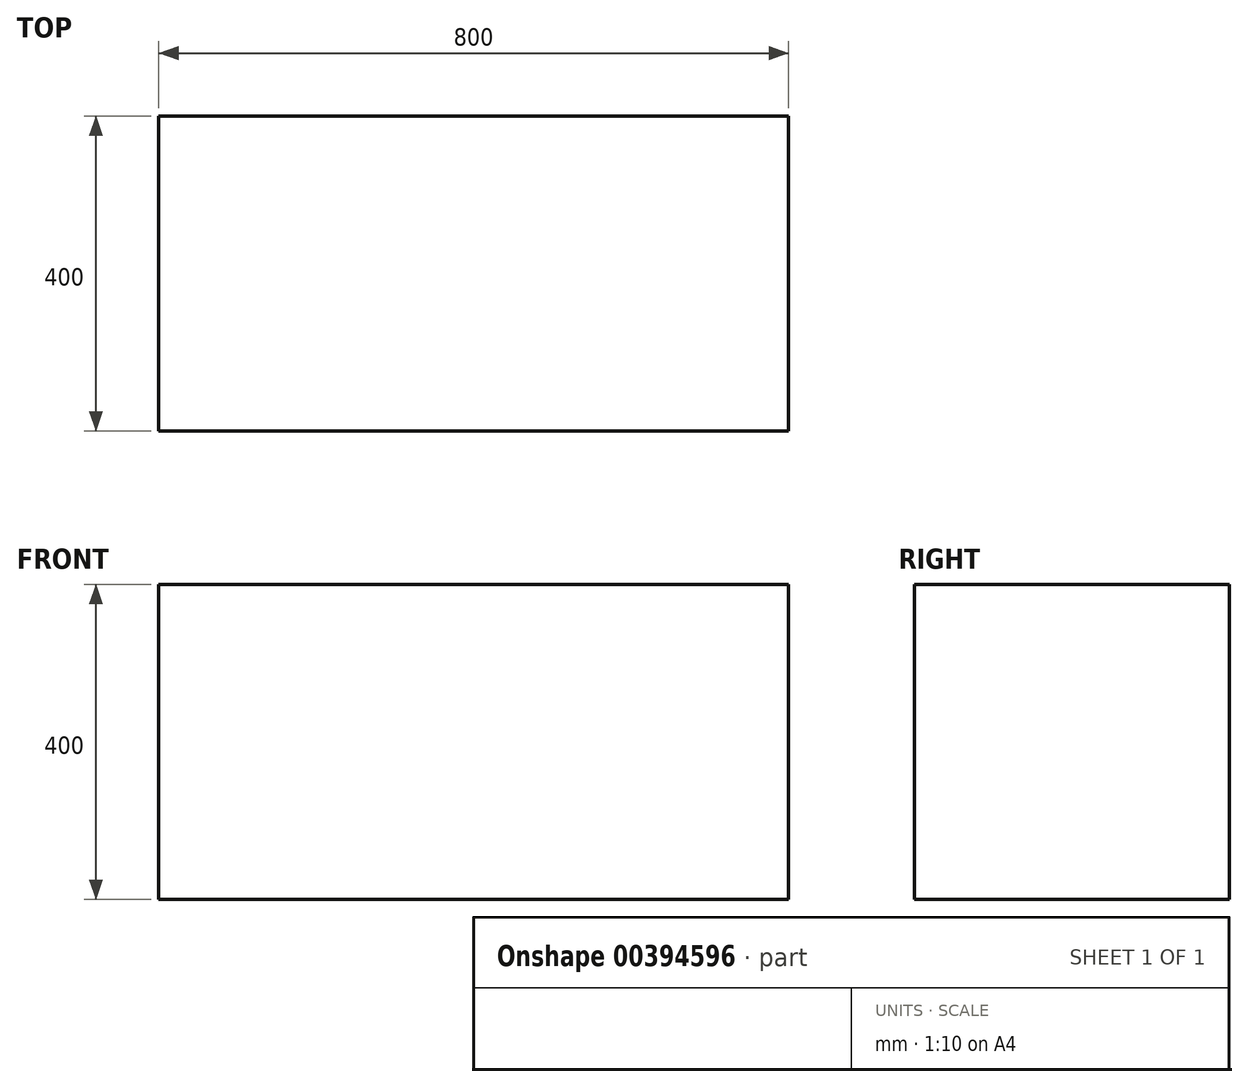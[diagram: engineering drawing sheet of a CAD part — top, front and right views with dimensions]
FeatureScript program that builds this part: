
annotation { "Feature Type Name" : "Feature", "Feature Type Description" : "" }
export const myFeature = defineFeature(function(context is Context, id is Id, definition is map)
    precondition{}
    {
        {
            var Q0;
            Q0=qCreatedBy(makeId("Front.planeOp"),FACE);
            var sketch = newSketch(context, id + "F0", { "sketchPlane" : qUnion([Q0])});
            skLineSegment(sketch, "E0.bottom", {"start": v(400, -200) * mm, "end": v(-400, -200) * mm});
            skLineSegment(sketch, "E0.top", {"start": v(400, 200) * mm, "end": v(-400, 200) * mm});
            skLineSegment(sketch, "E0.left", {"start": v(400, -200) * mm, "end": v(400, 200) * mm});
            skLineSegment(sketch, "E0.right", {"start": v(-400, -200) * mm, "end": v(-400, 200) * mm});
            skPoint(sketch, "E0.middle", {"position": v(0, 0) * mm});
            skSolve(sketch);
        }
        {
            var Q0;
            Q0=makeQuery(id+"F0.imprint","IMPRINT",FACE,{"disambiguationData":[TD([[makeQuery(id+"F0.imprint","IMPRINT",EDGE,{"derivedFrom":sQuery(id+"F0.wireOp",EDGE,"E0.bottom")}),-1.0]])]});
            extrude(context, id + "F1", {"entities" : qUnion([Q0]), "depth" : 400 * mm});
        }
    });
